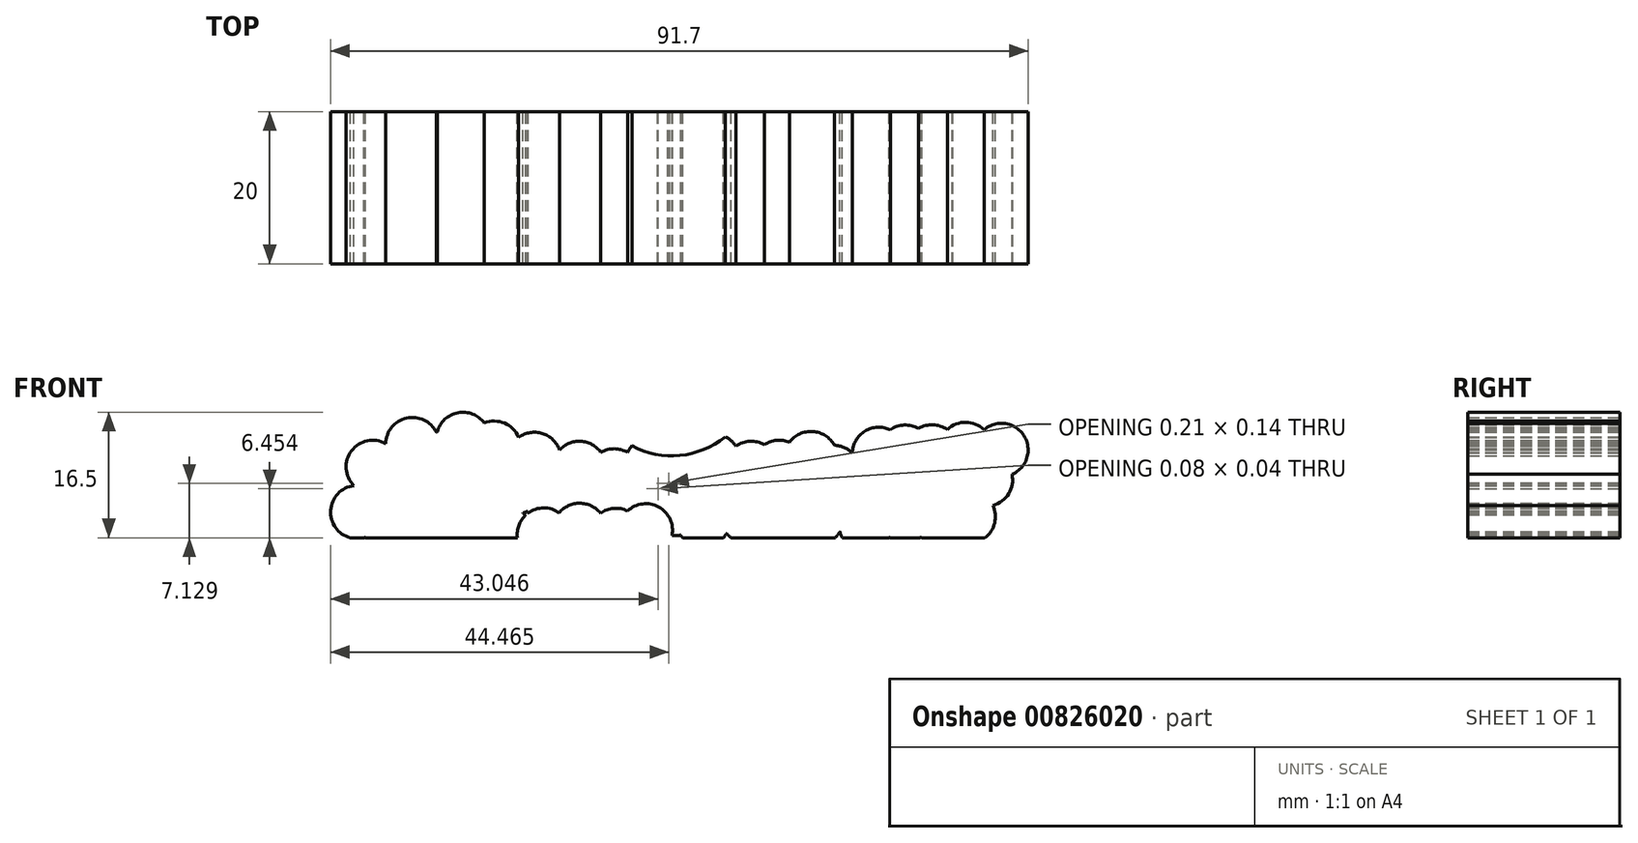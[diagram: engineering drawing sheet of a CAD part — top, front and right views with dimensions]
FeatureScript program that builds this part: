
annotation { "Feature Type Name" : "Feature", "Feature Type Description" : "" }
export const myFeature = defineFeature(function(context is Context, id is Id, definition is map)
    precondition{}
    {
        {
            var Q0;
            Q0=qCreatedBy(makeId("Front.planeOp"),FACE);
            var sketch = newSketch(context, id + "F0", { "sketchPlane" : qUnion([Q0])});
            skArc(sketch, "E0", {"start": v(-12.57, 14.53) * mm, "mid": v(-17.08, 13.6) * mm, "end": v(-16.77, 9.01) * mm});
            skArc(sketch, "E1.trimOffspring", {"start": v(-5.94, 16.04) * mm, "mid": v(-9.85, 17.9) * mm, "end": v(-12.57, 14.53) * mm});
            skLineSegment(sketch, "E2", {"start": v(-18.06, 2.16) * mm, "end": v(181.94, 2.16) * mm});
            skArc(sketch, "E3.trimOffspring", {"start": v(-9.29, 5.54) * mm, "mid": v(-9.21, 5.52) * mm, "end": v(-9.14, 5.5) * mm});
            skArc(sketch, "E4", {"start": v(0.38, 17.25) * mm, "mid": v(-3.08, 18.6) * mm, "end": v(-5.8, 16.08) * mm});
            skArc(sketch, "E5.trimOffspring", {"start": v(-5.8, 16.08) * mm, "mid": v(-5.87, 16.06) * mm, "end": v(-5.94, 16.04) * mm});
            skPoint(sketch, "E6.centerSnap0", {"position": v(-0.42, 10.37) * mm});
            skArc(sketch, "E7", {"start": v(5.42, 5.4) * mm, "mid": v(5.73, 5.5) * mm, "end": v(6.02, 5.64) * mm});
            skArc(sketch, "E8", {"start": v(4.9, 15.37) * mm, "mid": v(3.03, 17.23) * mm, "end": v(0.38, 17.25) * mm});
            skArc(sketch, "E9", {"start": v(6.02, 5.64) * mm, "mid": v(8.36, 3.78) * mm, "end": v(11.28, 4.4) * mm});
            skArc(sketch, "E10", {"start": v(15.7, 13.39) * mm, "mid": v(13.06, 14.85) * mm, "end": v(10.26, 13.7) * mm});
            skArc(sketch, "E11", {"start": v(11.28, 4.4) * mm, "mid": v(12.91, 3.73) * mm, "end": v(14.67, 3.93) * mm});
            skArc(sketch, "E12.trimOffspring", {"start": v(10.26, 13.7) * mm, "mid": v(8, 15.88) * mm, "end": v(4.9, 15.37) * mm});
            skArc(sketch, "E13", {"start": v(14.67, 3.93) * mm, "mid": v(17.7, 2.55) * mm, "end": v(20.5, 4.32) * mm});
            skArc(sketch, "E14", {"start": v(20.21, 8.2) * mm, "mid": v(20.22, 8.22) * mm, "end": v(20.24, 8.23) * mm});
            skPoint(sketch, "E6.center.orphan", {"position": v(-0.42, 11.2) * mm});
            skArc(sketch, "E15", {"start": v(23.18, 8.6) * mm, "mid": v(23.22, 8.6) * mm, "end": v(23.25, 8.6) * mm});
            skArc(sketch, "E16.trimOffspring", {"start": v(19.24, 13.37) * mm, "mid": v(17.47, 13.86) * mm, "end": v(15.7, 13.39) * mm});
            skArc(sketch, "E17", {"start": v(27.52, 14.05) * mm, "mid": v(26.3, 14.46) * mm, "end": v(25.03, 14.4) * mm});
            skArc(sketch, "E18", {"start": v(20.5, 4.32) * mm, "mid": v(21.42, 4.2) * mm, "end": v(22.34, 4.32) * mm});
            skArc(sketch, "E19", {"start": v(24.74, 9.36) * mm, "mid": v(24.63, 9.33) * mm, "end": v(24.53, 9.3) * mm});
            skArc(sketch, "E20.trimOffspring", {"start": v(25.03, 14.4) * mm, "mid": v(21.86, 15.47) * mm, "end": v(19.24, 13.37) * mm});
            skArc(sketch, "E21.trimOffspring", {"start": v(24.57, 9.22) * mm, "mid": v(24.55, 9.26) * mm, "end": v(24.53, 9.3) * mm});
            skArc(sketch, "E22.trimOffspring", {"start": v(24.57, 9.22) * mm, "mid": v(24.66, 9.29) * mm, "end": v(24.74, 9.36) * mm});
            skArc(sketch, "E23.trimOffspring", {"start": v(23.23, 8.64) * mm, "mid": v(23.2, 8.61) * mm, "end": v(23.18, 8.6) * mm});
            skArc(sketch, "E24.trimOffspring", {"start": v(23.23, 8.64) * mm, "mid": v(23.24, 8.62) * mm, "end": v(23.25, 8.6) * mm});
            skArc(sketch, "E25.trimOffspring", {"start": v(22.34, 4.32) * mm, "mid": v(23.96, 2.76) * mm, "end": v(26.2, 2.5) * mm});
            skArc(sketch, "E26", {"start": v(24.7, 9.35) * mm, "mid": v(24.7, 9.33) * mm, "end": v(24.69, 9.31) * mm});
            skArc(sketch, "E27", {"start": v(26.2, 2.5) * mm, "mid": v(26.32, 2.33) * mm, "end": v(26.45, 2.16) * mm});
            skArc(sketch, "E28", {"start": v(33.45, 14.2) * mm, "mid": v(30.44, 15.77) * mm, "end": v(27.52, 14.05) * mm});
            skArc(sketch, "E29", {"start": v(32.21, 2.74) * mm, "mid": v(32.5, 2.43) * mm, "end": v(32.84, 2.16) * mm});
            skArc(sketch, "E30", {"start": v(36.28, 2.16) * mm, "mid": v(36.36, 2.02) * mm, "end": v(36.45, 1.88) * mm});
            skArc(sketch, "E31.trimOffspring", {"start": v(37.2, 14.4) * mm, "mid": v(35.3, 14.85) * mm, "end": v(33.45, 14.2) * mm});
            skArc(sketch, "E32.trimOffspring", {"start": v(39.13, 11.48) * mm, "mid": v(39.05, 11.5) * mm, "end": v(38.98, 11.5) * mm});
            skArc(sketch, "E33.trimOffspring", {"start": v(41.79, 9.2) * mm, "mid": v(41.87, 9.3) * mm, "end": v(41.96, 9.42) * mm});
            skPoint(sketch, "E34.orphan", {"position": v(36.62, 8.04) * mm});
            skArc(sketch, "E35", {"start": v(46.48, 7.12) * mm, "mid": v(46.55, 7.22) * mm, "end": v(46.62, 7.33) * mm});
            skCircle(sketch, "E36", {"center": v(123.24, 11.12) * mm, "radius": 3.5 * mm});
            skCircle(sketch, "E37", {"center": v(161.86, 17.52) * mm, "radius": 3.5 * mm});
            skArc(sketch, "E38", {"start": v(48.76, 13.31) * mm, "mid": v(47.67, 14.04) * mm, "end": v(46.4, 14.31) * mm});
            skArc(sketch, "E39.trimOffspring", {"start": v(40.5, 14.7) * mm, "mid": v(38.8, 14.97) * mm, "end": v(37.2, 14.4) * mm});
            skArc(sketch, "E40.trimOffspring", {"start": v(46.4, 14.31) * mm, "mid": v(43.55, 16.13) * mm, "end": v(40.5, 14.7) * mm});
            skArc(sketch, "E41.trimOffspring", {"start": v(46.3, 10.81) * mm, "mid": v(46.4, 10.99) * mm, "end": v(46.5, 11.16) * mm});
            skArc(sketch, "E42.trimOffspring", {"start": v(55.76, 13.23) * mm, "mid": v(55.75, 13.36) * mm, "end": v(55.74, 13.48) * mm});
            skArc(sketch, "E43.trimOffspring", {"start": v(53.75, 16.36) * mm, "mid": v(50.43, 16.18) * mm, "end": v(48.76, 13.31) * mm});
            skArc(sketch, "E44.trimOffspring", {"start": v(57.46, 16.53) * mm, "mid": v(55.58, 16.98) * mm, "end": v(53.75, 16.36) * mm});
            skArc(sketch, "E45", {"start": v(47.12, 3) * mm, "mid": v(47.25, 2.57) * mm, "end": v(47.44, 2.16) * mm});
            skArc(sketch, "E46", {"start": v(57.65, 2.16) * mm, "mid": v(57.71, 2.2) * mm, "end": v(57.77, 2.25) * mm});
            skArc(sketch, "E47.trimOffspring", {"start": v(53.59, 2.16) * mm, "mid": v(53.6, 2.2) * mm, "end": v(53.63, 2.23) * mm});
            skArc(sketch, "E48.trimOffspring", {"start": v(46.51, 2.16) * mm, "mid": v(46.84, 2.55) * mm, "end": v(47.12, 3) * mm});
            skArc(sketch, "E49.trimOffspring", {"start": v(36.45, 1.88) * mm, "mid": v(36.69, 2.01) * mm, "end": v(36.91, 2.16) * mm});
            skArc(sketch, "E50.trimOffspring", {"start": v(31.82, 2.16) * mm, "mid": v(32.03, 2.44) * mm, "end": v(32.21, 2.74) * mm});
            skArc(sketch, "E51.trimOffspring", {"start": v(53.63, 2.23) * mm, "mid": v(53.68, 2.2) * mm, "end": v(53.73, 2.16) * mm});
            skArc(sketch, "E52", {"start": v(57.77, 2.25) * mm, "mid": v(57.83, 2.2) * mm, "end": v(57.89, 2.16) * mm});
            skArc(sketch, "E53.trimOffspring", {"start": v(61.24, 16.4) * mm, "mid": v(59.37, 17.02) * mm, "end": v(57.46, 16.53) * mm});
            skArc(sketch, "E54.trimOffspring", {"start": v(61.9, 2.16) * mm, "mid": v(61.91, 2.17) * mm, "end": v(61.92, 2.17) * mm});
            skArc(sketch, "E55", {"start": v(66.19, 2.16) * mm, "mid": v(67.46, 4.1) * mm, "end": v(67.24, 6.42) * mm});
            skArc(sketch, "E56", {"start": v(67.24, 6.42) * mm, "mid": v(69.3, 7.96) * mm, "end": v(69.75, 10.5) * mm});
            skArc(sketch, "E57", {"start": v(69.75, 10.5) * mm, "mid": v(71.33, 15.57) * mm, "end": v(66.08, 16.36) * mm});
            skArc(sketch, "E58.trimOffspring", {"start": v(66.08, 16.36) * mm, "mid": v(63.67, 17.34) * mm, "end": v(61.24, 16.4) * mm});
            skArc(sketch, "E59.trimOffspring", {"start": v(61.92, 2.17) * mm, "mid": v(61.93, 2.17) * mm, "end": v(61.94, 2.16) * mm});
            skCircle(sketch, "E60", {"center": v(21.62, 3.14) * mm, "radius": 3.5 * mm});
            skCircle(sketch, "E61", {"center": v(12.91, 3.2) * mm, "radius": 3.5 * mm});
            skPoint(sketch, "E61.centerSnap0", {"position": v(12.91, 3.73) * mm});
            skArc(sketch, "E62", {"start": v(0.6, 2.16) * mm, "mid": v(6.05, -0.74) * mm, "end": v(5.42, 5.4) * mm});
            skArc(sketch, "E63", {"start": v(19.77, 14.25) * mm, "mid": v(26.09, 12.99) * mm, "end": v(32.04, 15.43) * mm});
            skArc(sketch, "E64", {"start": v(-16.77, 9.01) * mm, "mid": v(-19.82, 5.78) * mm, "end": v(-17.24, 2.16) * mm});
            skArc(sketch, "E65", {"start": v(-15.27, 2.2) * mm, "mid": v(-15.26, 2.18) * mm, "end": v(-15.25, 2.16) * mm});
            skArc(sketch, "E66", {"start": v(0.91, 0.71) * mm, "mid": v(1.27, 1.4) * mm, "end": v(1.47, 2.16) * mm});
            skCircle(sketch, "E67", {"center": v(8.2, 2.59) * mm, "radius": 3.5 * mm});
            skCircle(sketch, "E68", {"center": v(17.7, 2.55) * mm, "radius": 3.5 * mm});
            skArc(sketch, "E69.trimOffspring", {"start": v(-9.14, 5.5) * mm, "mid": v(-9.27, 5.68) * mm, "end": v(-9.42, 5.86) * mm});
            skArc(sketch, "E70.trimOffspring", {"start": v(-15.42, 2.16) * mm, "mid": v(-15.34, 2.18) * mm, "end": v(-15.27, 2.2) * mm});
            skArc(sketch, "E71.trimOffspring", {"start": v(0.68, 1.41) * mm, "mid": v(1.82, 1.6) * mm, "end": v(2.84, 2.16) * mm});
            skSolve(sketch);
        }
        {
            var Q0;
            Q0=makeQuery(id+"F0.imprint","IMPRINT",FACE,{"disambiguationData":[TD([[makeQuery(id+"F0.imprint","IMPRINT",EDGE,{"derivedFrom":sQuery(id+"F0.wireOp",EDGE,"E0")}),1.0]])]});
            extrude(context, id + "F1", {"entities" : qUnion([Q0]), "depth" : 20 * mm, "offsetDistance" : 25 * mm});
        }
    });
